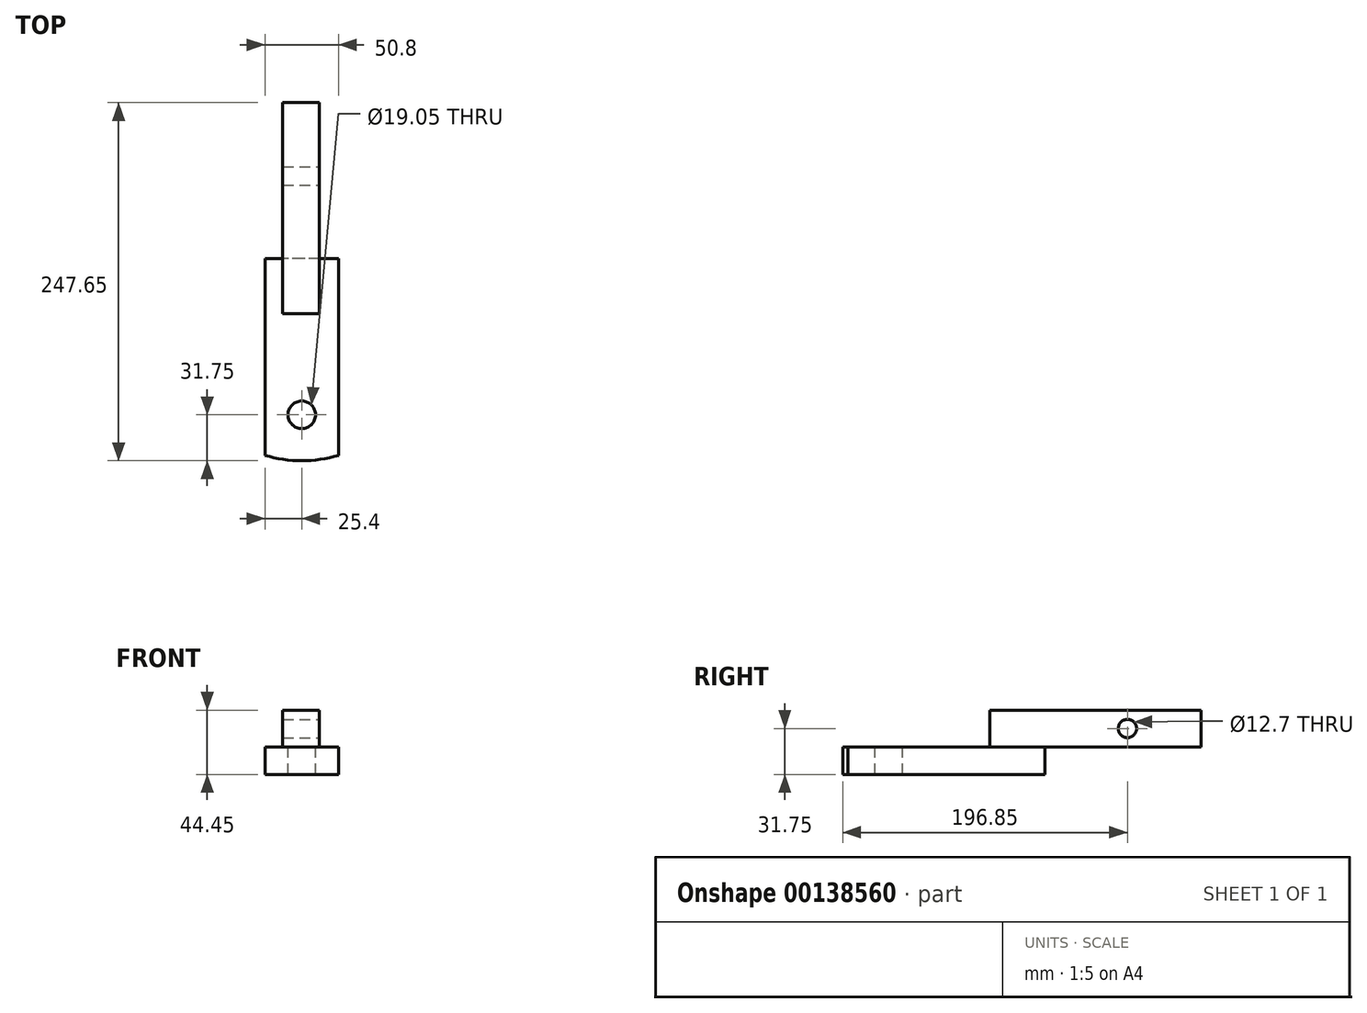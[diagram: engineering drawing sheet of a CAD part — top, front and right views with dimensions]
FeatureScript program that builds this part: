
annotation { "Feature Type Name" : "Feature", "Feature Type Description" : "" }
export const myFeature = defineFeature(function(context is Context, id is Id, definition is map)
    precondition{}
    {
        {
            var Q0;
            Q0=qCreatedBy(makeId("Top.planeOp"),FACE);
            var sketch = newSketch(context, id + "F0", { "sketchPlane" : qUnion([Q0])});
            skLineSegment(sketch, "E0.bottom", {"start": v(-13.11, 0) * mm, "end": v(12.29, 0) * mm});
            skLineSegment(sketch, "E0.top", {"start": v(-13.11, 146.05) * mm, "end": v(12.29, 146.05) * mm});
            skLineSegment(sketch, "E0.left", {"start": v(-13.11, 0) * mm, "end": v(-13.11, 146.05) * mm});
            skLineSegment(sketch, "E0.right", {"start": v(12.29, 0) * mm, "end": v(12.29, 146.05) * mm});
            skSolve(sketch);
        }
        {
            var Q0;
            Q0 = qSketchRegion(id + "F0", true);
            extrude(context, id + "F1", {"entities" : qUnion([Q0]), "depth" : 25.4 * mm});
        }
        {
            var Q0;
            Q0=qCreatedBy(makeId("Top.planeOp"),FACE);
            var sketch = newSketch(context, id + "F2", { "sketchPlane" : qUnion([Q0])});
            skLineSegment(sketch, "E1", {"start": v(0, 38.1) * mm, "end": v(-25.4, 38.1) * mm});
            skLineSegment(sketch, "E2", {"start": v(-25.4, 38.1) * mm, "end": v(-25.4, -97.87) * mm});
            skLineSegment(sketch, "E3", {"start": v(25.4, -97.87) * mm, "end": v(25.4, 38.1) * mm});
            skLineSegment(sketch, "E4", {"start": v(25.4, 38.1) * mm, "end": v(0, 38.1) * mm});
            skArc(sketch, "E5", {"start": v(-25.4, -97.87) * mm, "mid": v(0, -101.6) * mm, "end": v(25.4, -97.87) * mm});
            skPoint(sketch, "E5.centerSnap0", {"position": v(0, -101.6) * mm});
            skPoint(sketch, "E6.orphan", {"position": v(25.4, -101.6) * mm});
            skPoint(sketch, "E7.orphan", {"position": v(-25.4, -101.6) * mm});
            skSolve(sketch);
        }
        {
            var Q0;
            Q0 = qSketchRegion(id + "F2", true);
            extrude(context, id + "F3", {"entities" : qUnion([Q0]), "operationType" : NewBodyOperationType.ADD, "oppositeDirection" : true, "depth" : 19.05 * mm});
        }
        {
            var Q0;
            Q0=makeQuery(id+"F1.opExtrude","SWEPT_FACE",FACE,{"disambiguationData":[OSD([sQuery(id+"F0.wireOp",EDGE,"E0.right")])]});
            var sketch = newSketch(context, id + "F4", { "sketchPlane" : qUnion([Q0])});
            skLineSegment(sketch, "E8.0", {"start": v(146.05, 25.4) * mm, "end": v(146.05, 0) * mm});
            skCircle(sketch, "E9", {"center": v(95.25, 12.7) * mm, "radius": 6.35 * mm});
            skPoint(sketch, "E9.centerSnap0", {"position": v(146.05, 12.7) * mm});
            skSolve(sketch);
        }
        {
            var Q0;
            Q0 = qSketchRegion(id + "F4", true);
            extrude(context, id + "F5", {"entities" : qUnion([Q0]), "operationType" : NewBodyOperationType.REMOVE, "endBound" : BoundingType.THROUGH_ALL, "oppositeDirection" : true, "depth" : 25.4 * mm});
        }
        {
            var Q0;
            Q0=makeQuery(id+"F3.opExtrude","CAP_FACE",FACE,{"disambiguationData":[OSD([sQuery(id+"F2.wireOp",EDGE,"E1"),sQuery(id+"F2.wireOp",EDGE,"E2"),sQuery(id+"F2.wireOp",EDGE,"E3"),sQuery(id+"F2.wireOp",EDGE,"E4"),sQuery(id+"F2.wireOp",EDGE,"E5")])],"isStart":true});
            var sketch = newSketch(context, id + "F6", { "sketchPlane" : qUnion([Q0])});
            skCircle(sketch, "E10", {"center": v(0, -69.85) * mm, "radius": 9.53 * mm});
            skPoint(sketch, "E10.centerSnap0", {"position": v(0, -101.6) * mm});
            skSolve(sketch);
        }
        {
            var Q0;
            Q0 = qSketchRegion(id + "F6", true);
            extrude(context, id + "F7", {"entities" : qUnion([Q0]), "operationType" : NewBodyOperationType.REMOVE, "oppositeDirection" : true, "depth" : 25.4 * mm});
        }
    });
